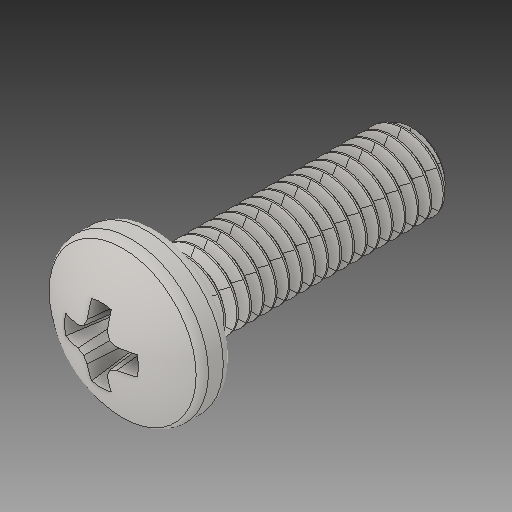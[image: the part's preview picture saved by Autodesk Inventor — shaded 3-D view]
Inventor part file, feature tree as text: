
AUTODESK INVENTOR PART (.ipt)
format: ipt  version: 2019 (Build 230136000, 136)  size: 1,118,208 bytes
history: imported  units: mm
features: imported_body x1
ambient origin geometry x8: Origin, YZ Plane, XZ Plane, XY Plane, X Axis, Y Axis, Z Axis, Center Point
bodies: Solide1 (imported_parasolid), Body1 (imported_parasolid)
feature tree (1):
  imported_body  NMx_Import_Brep_tag  [imported B-rep: ~6 faces, bbox_mm=None]
